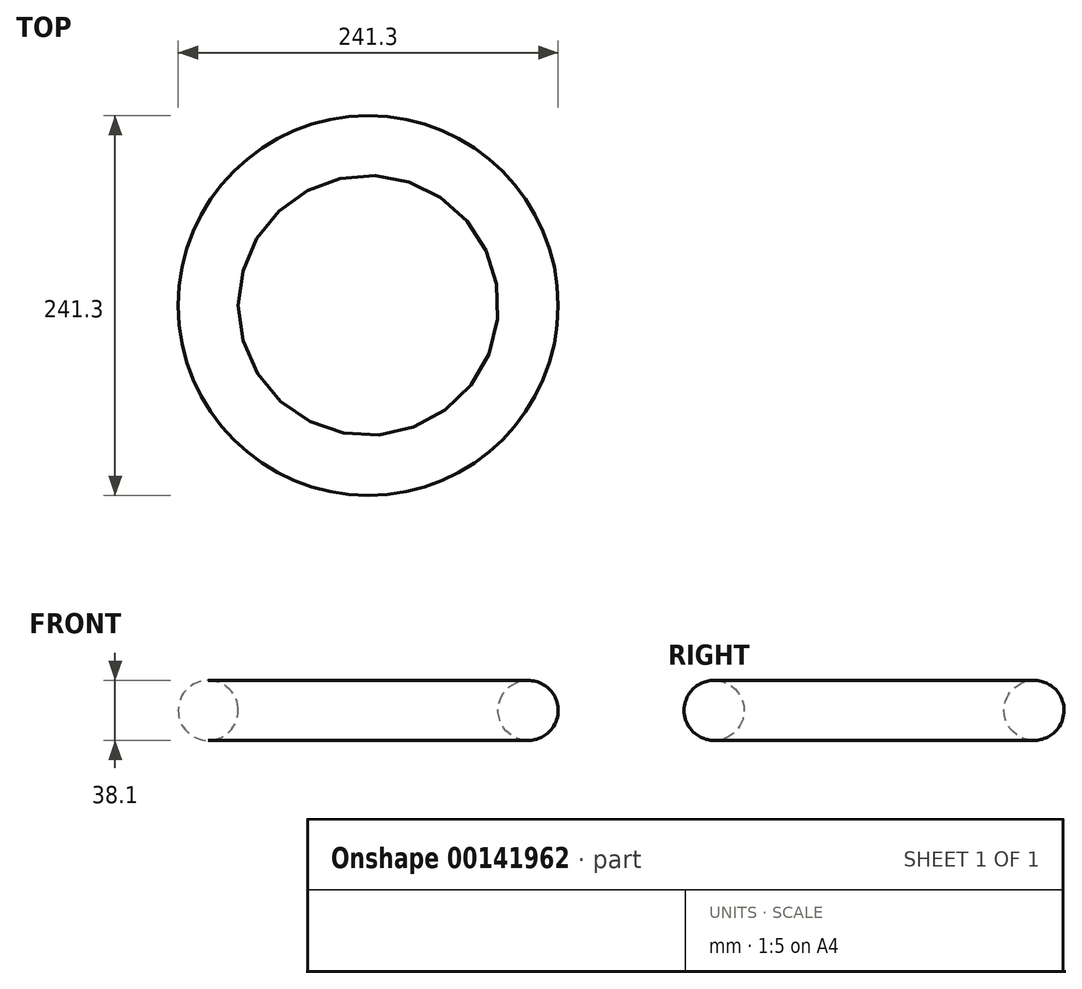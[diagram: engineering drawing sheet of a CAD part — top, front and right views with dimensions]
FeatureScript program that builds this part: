
annotation { "Feature Type Name" : "Feature", "Feature Type Description" : "" }
export const myFeature = defineFeature(function(context is Context, id is Id, definition is map)
    precondition{}
    {
        {
            var Q0;
            Q0=qCreatedBy(makeId("Front.planeOp"),FACE);
            var sketch = newSketch(context, id + "F0", { "sketchPlane" : qUnion([Q0])});
            skCircle(sketch, "E0", {"center": v(-101.6, 0) * mm, "radius": 19.05 * mm});
            skLineSegment(sketch, "E1", {"start": v(0, 0) * mm, "end": v(0, 83.52) * mm, "construction": true});
            skSolve(sketch);
        }
        {
            var Q0;
            Q0=makeQuery(id+"F0.imprint","IMPRINT",FACE,{"disambiguationData":[TD([[makeQuery(id+"F0.imprint","IMPRINT",EDGE,{"derivedFrom":sQuery(id+"F0.wireOp",EDGE,"E0")}),1.0]])]});
            var Q1;
            Q1=sQuery(id+"F0.wireOp",EDGE,"E1");
            revolve(context, id + "F1", {"entities" : qUnion([Q0]), "axis" : qUnion([Q1]), "revolveType" : RevolveType.FULL});
        }
    });
